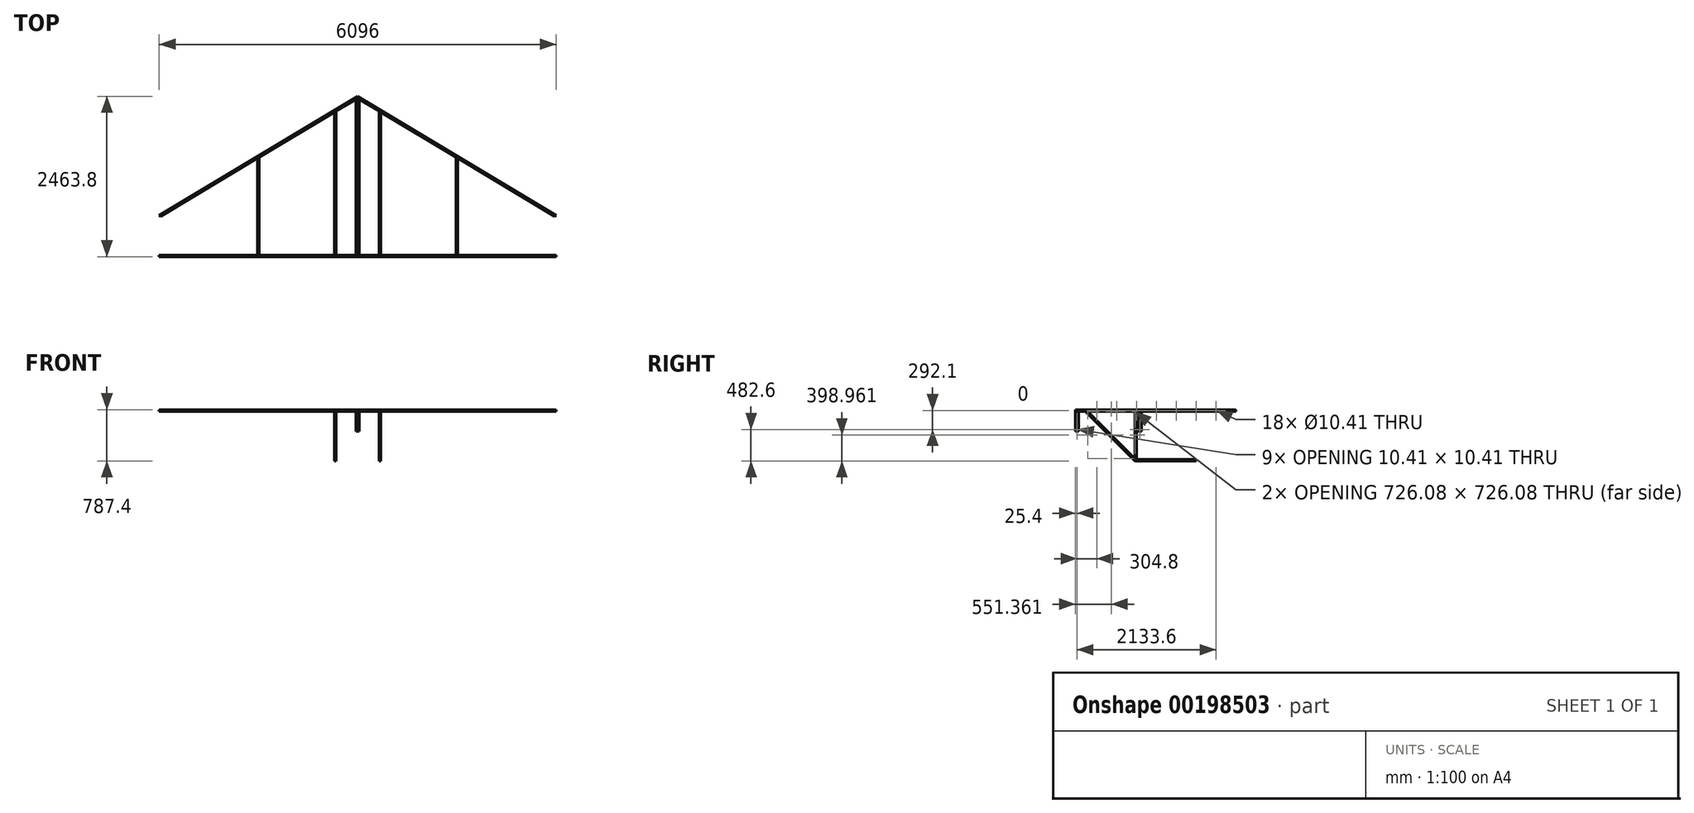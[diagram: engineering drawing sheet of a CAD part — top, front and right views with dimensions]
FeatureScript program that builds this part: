
annotation { "Feature Type Name" : "Feature", "Feature Type Description" : "" }
export const myFeature = defineFeature(function(context is Context, id is Id, definition is map)
    precondition{}
    {
        {
            var Q0;
            Q0=qCreatedBy(makeId("Top.planeOp"),FACE);
            var sketch = newSketch(context, id + "F0", { "sketchPlane" : qUnion([Q0])});
            skLineSegment(sketch, "E0.bottom", {"start": v(0, 0) * mm, "end": v(3048, 0) * mm});
            skLineSegment(sketch, "E0.top", {"start": v(0, 25.4) * mm, "end": v(3048, 25.4) * mm});
            skLineSegment(sketch, "E0.left", {"start": v(0, 0) * mm, "end": v(0, 25.4) * mm});
            skLineSegment(sketch, "E0.right", {"start": v(3048, 0) * mm, "end": v(3048, 25.4) * mm});
            skLineSegment(sketch, "E1.bottom", {"start": v(3048, 25.4) * mm, "end": v(3022.6, 25.4) * mm});
            skLineSegment(sketch, "E1.left", {"start": v(3048, 25.4) * mm, "end": v(3048, 635) * mm});
            skLineSegment(sketch, "E1.right", {"start": v(3022.6, 25.4) * mm, "end": v(3022.6, 620.62) * mm});
            skLineSegment(sketch, "E2", {"start": v(3048, 635) * mm, "end": v(3022.6, 620.62) * mm});
            skLineSegment(sketch, "E3", {"start": v(3048, 635) * mm, "end": v(0, 2463.8) * mm});
            skLineSegment(sketch, "E4", {"start": v(3022.6, 620.62) * mm, "end": v(25.4, 2418.94) * mm});
            skLineSegment(sketch, "E5", {"start": v(0, 25.4) * mm, "end": v(0, 2463.8) * mm});
            skLineSegment(sketch, "E6", {"start": v(0, 2463.8) * mm, "end": v(25.4, 2418.94) * mm});
            skLineSegment(sketch, "E7", {"start": v(25.4, 2418.94) * mm, "end": v(25.4, 25.4) * mm});
            skLineSegment(sketch, "E8", {"start": v(1511.3, 25.4) * mm, "end": v(1511.3, 1527.4) * mm});
            skLineSegment(sketch, "E9", {"start": v(1536.7, 1512.16) * mm, "end": v(1536.7, 25.4) * mm});
            skLineSegment(sketch, "E10", {"start": v(1511.3, 683.13) * mm, "end": v(1536.7, 683.13) * mm, "construction": true});
            skLineSegment(sketch, "E11", {"start": v(1524, 683.13) * mm, "end": v(1524, 25.4) * mm, "construction": true});
            skLineSegment(sketch, "E12", {"start": v(330.2, 25.4) * mm, "end": v(330.2, 2236.06) * mm});
            skLineSegment(sketch, "E13", {"start": v(355.6, 25.4) * mm, "end": v(355.6, 2220.82) * mm});
            skSolve(sketch);
        }
        {
            var Q0;
            {var subQ0=sQuery(id+"F0.wireOp",EDGE,"E5");Q0=makeQuery(id+"F0.imprint","IMPRINT",FACE,{"disambiguationData":[TD([[makeQuery(id+"F0.imprint","IMPRINT",EDGE,{"derivedFrom":subQ0}),-1.0]])]});}
            var Q1;
            {var subQ3=sQuery(id+"F0.wireOp",EDGE,"E2");Q1=makeQuery(id+"F0.imprint","IMPRINT",FACE,{"disambiguationData":[TD([[makeQuery(id+"F0.imprint","IMPRINT",EDGE,{"derivedFrom":subQ3}),-1.0]])]});}
            var Q2;
            {var subQ0=sQuery(id+"F0.wireOp",EDGE,"E8");Q2=makeQuery(id+"F0.imprint","IMPRINT",FACE,{"disambiguationData":[TD([[makeQuery(id+"F0.imprint","IMPRINT",EDGE,{"derivedFrom":subQ0}),-1.0]])]});}
            var Q3;
            Q3=makeQuery(id+"F0.imprint","IMPRINT",FACE,{"disambiguationData":[TD([[makeQuery(id+"F0.imprint","IMPRINT",EDGE,{"derivedFrom":sQuery(id+"F0.wireOp",EDGE,"E1.bottom")}),-1.0]])]});
            var Q4;
            Q4=makeQuery(id+"F0.imprint","IMPRINT",FACE,{"disambiguationData":[TD([[makeQuery(id+"F0.imprint","IMPRINT",EDGE,{"derivedFrom":sQuery(id+"F0.wireOp",EDGE,"E0.bottom")}),1.0]])]});
            var Q5;
            {var subQ0=sQuery(id+"F0.wireOp",EDGE,"E12");Q5=makeQuery(id+"F0.imprint","IMPRINT",FACE,{"disambiguationData":[TD([[makeQuery(id+"F0.imprint","IMPRINT",EDGE,{"derivedFrom":subQ0}),-1.0]])]});}
            extrude(context, id + "F1", {"entities" : qUnion([Q0, Q1, Q2, Q3, Q4, Q5]), "depth" : 25.4 * mm});
        }
        {
            var Q0;
            Q0=makeQuery(id+"F1.opExtrude","SWEPT_FACE",FACE,{"disambiguationData":[OSD([sQuery(id+"F0.wireOp",EDGE,"E0.bottom")])]});
            var sketch = newSketch(context, id + "F2", { "sketchPlane" : qUnion([Q0])});
            skLineSegment(sketch, "E14.0", {"start": v(0, 0) * mm, "end": v(3048, 0) * mm});
            skLineSegment(sketch, "E15", {"start": v(0, 0) * mm, "end": v(0, -304.8) * mm});
            skLineSegment(sketch, "E16", {"start": v(0, -304.8) * mm, "end": v(25.4, -304.8) * mm});
            skLineSegment(sketch, "E17", {"start": v(25.4, -304.8) * mm, "end": v(25.4, 0) * mm});
            skLineSegment(sketch, "E18", {"start": v(25.4, -279.4) * mm, "end": v(304.8, 0) * mm});
            skLineSegment(sketch, "E19", {"start": v(25.4, -243.48) * mm, "end": v(268.88, 0) * mm});
            skSolve(sketch);
        }
        {
            var Q0;
            {var subQ3=sQuery(id+"F2.wireOp",EDGE,"E15");Q0=makeQuery(id+"F2.imprint","IMPRINT",FACE,{"disambiguationData":[TD([[makeQuery(id+"F2.imprint","IMPRINT",EDGE,{"derivedFrom":subQ3}),1.0]])]});}
            extrude(context, id + "F3", {"entities" : qUnion([Q0]), "operationType" : NewBodyOperationType.ADD, "oppositeDirection" : true, "depth" : 50.8 * mm});
        }
        {
            var Q0;
            Q0=makeQuery(id+"F3.opExtrude","CAP_FACE",FACE,{"disambiguationData":[OSD([sQuery(id+"F2.wireOp",EDGE,"E14.0"),sQuery(id+"F2.wireOp",EDGE,"E15"),sQuery(id+"F2.wireOp",EDGE,"E16"),sQuery(id+"F2.wireOp",EDGE,"E17")])],"isStart":false});
            cPlane(context, id + "F4", {"entities" : qUnion([Q0]), "cplaneType" : CPlaneType.OFFSET, "offset" : 914.4 * mm, "width" : 152.4 * mm, "height" : 152.4 * mm});
        }
        {
            var Q0;
            Q0=qCreatedBy(id+"F4.planeOp",FACE);
            var sketch = newSketch(context, id + "F5", { "sketchPlane" : qUnion([Q0])});
            skLineSegment(sketch, "E20.0.0", {"start": v(0, 0) * mm, "end": v(-25.4, 0) * mm});
            skLineSegment(sketch, "E20.0.1", {"start": v(-25.4, 0) * mm, "end": v(-25.4, -304.8) * mm});
            skLineSegment(sketch, "E20.0.2", {"start": v(-25.4, -304.8) * mm, "end": v(0, -304.8) * mm});
            skLineSegment(sketch, "E20.0.3", {"start": v(0, -304.8) * mm, "end": v(0, 0) * mm});
            skSolve(sketch);
        }
        {
            var Q0;
            Q0 = qSketchRegion(id + "F5", true);
            extrude(context, id + "F6", {"entities" : qUnion([Q0]), "operationType" : NewBodyOperationType.ADD, "depth" : 50.8 * mm});
        }
        {
            var Q0;
            Q0=makeQuery(id+"F1.opExtrude","SWEPT_FACE",FACE,{"disambiguationData":[OSD([sQuery(id+"F0.wireOp",EDGE,"E12")])]});
            var sketch = newSketch(context, id + "F7", { "sketchPlane" : qUnion([Q0])});
            skLineSegment(sketch, "E21.0", {"start": v(-25.4, 0) * mm, "end": v(-2236.06, 0) * mm});
            skLineSegment(sketch, "E22", {"start": v(-939.8, 0) * mm, "end": v(-939.8, -762) * mm});
            skLineSegment(sketch, "E23", {"start": v(-939.8, -762) * mm, "end": v(-914.4, -762) * mm});
            skLineSegment(sketch, "E24", {"start": v(-914.4, -762) * mm, "end": v(-914.4, 0) * mm});
            skLineSegment(sketch, "E25", {"start": v(-914.4, -762) * mm, "end": v(-152.4, 0) * mm});
            skLineSegment(sketch, "E26", {"start": v(-152.4, 0) * mm, "end": v(-188.32, 0) * mm});
            skLineSegment(sketch, "E27", {"start": v(-188.32, 0) * mm, "end": v(-914.4, -726.08) * mm});
            skLineSegment(sketch, "E28", {"start": v(-939.8, -762) * mm, "end": v(-1854.2, -762) * mm});
            skLineSegment(sketch, "E29", {"start": v(-1854.2, -762) * mm, "end": v(-1854.2, -736.6) * mm});
            skLineSegment(sketch, "E30", {"start": v(-1854.2, -736.6) * mm, "end": v(-939.8, -736.6) * mm});
            skSolve(sketch);
        }
        {
            var Q0;
            {var subQ0=sQuery(id+"F7.wireOp",EDGE,"E25");Q0=makeQuery(id+"F7.imprint","IMPRINT",FACE,{"disambiguationData":[TD([[makeQuery(id+"F7.imprint","IMPRINT",EDGE,{"derivedFrom":subQ0}),1.0]])]});}
            var Q1;
            {var subQ0=sQuery(id+"F7.wireOp",EDGE,"E23");Q1=makeQuery(id+"F7.imprint","IMPRINT",FACE,{"disambiguationData":[TD([[makeQuery(id+"F7.imprint","IMPRINT",EDGE,{"derivedFrom":subQ0}),1.0]])]});}
            var Q2;
            {var subQ0=sQuery(id+"F7.wireOp",EDGE,"E28");Q2=makeQuery(id+"F7.imprint","IMPRINT",FACE,{"disambiguationData":[TD([[makeQuery(id+"F7.imprint","IMPRINT",EDGE,{"derivedFrom":subQ0}),-1.0]])]});}
            extrude(context, id + "F8", {"entities" : qUnion([Q0, Q1, Q2]), "operationType" : NewBodyOperationType.ADD, "oppositeDirection" : true, "depth" : 25.4 * mm});
        }
        {
            var Q0;
            Q0=makeQuery(id+"F6.boolean.opBoolean","MERGE",FACE,{"derivedFrom":[makeQuery(id+"F3.boolean.opBoolean","MERGE",FACE,{"derivedFrom":[makeQuery(id+"F1.opExtrude","SWEPT_FACE",FACE,{"disambiguationData":[OSD([sQuery(id+"F0.wireOp",EDGE,"E0.left"),sQuery(id+"F0.wireOp",EDGE,"E5")])]}),makeQuery(id+"F3.opExtrude","SWEPT_FACE",FACE,{"disambiguationData":[OSD([sQuery(id+"F2.wireOp",EDGE,"E15")])]})]}),makeQuery(id+"F6.opExtrude","SWEPT_FACE",FACE,{"disambiguationData":[OSD([sQuery(id+"F5.wireOp",EDGE,"E20.0.3")])]})]});
            var sketch = newSketch(context, id + "F9", { "sketchPlane" : qUnion([Q0])});
            skLineSegment(sketch, "E31", {"start": v(-2463.8, 12.7) * mm, "end": v(0, 12.7) * mm, "construction": true});
            skLineSegment(sketch, "E32", {"start": v(-25.4, -304.8) * mm, "end": v(-25.4, 25.4) * mm, "construction": true});
            skLineSegment(sketch, "E33", {"start": v(-990.6, -304.8) * mm, "end": v(-990.6, 25.4) * mm, "construction": true});
            skCircle(sketch, "E34", {"center": v(-2159, 12.7) * mm, "radius": 5.2 * mm});
            skCircle(sketch, "E35.1.0.0", {"center": v(-1854.2, 12.7) * mm, "radius": 5.2 * mm});
            skCircle(sketch, "E35.2.0.0", {"center": v(-1549.4, 12.7) * mm, "radius": 5.2 * mm});
            skLineSegment(sketch, "E35.direction1", {"start": v(-2159, 12.7) * mm, "end": v(-1854.2, 12.7) * mm, "construction": true});
            skCircle(sketch, "E36.0.3.0", {"center": v(-1244.6, 12.7) * mm, "radius": 5.2 * mm});
            skCircle(sketch, "E36.0.4.0", {"center": v(-939.8, 12.7) * mm, "radius": 5.2 * mm});
            skCircle(sketch, "E36.0.5.0", {"center": v(-635, 12.7) * mm, "radius": 5.2 * mm});
            skCircle(sketch, "E36.0.6.0", {"center": v(-330.2, 12.7) * mm, "radius": 5.2 * mm});
            skCircle(sketch, "E37", {"center": v(-990.6, -279.4) * mm, "radius": 5.2 * mm});
            skCircle(sketch, "E38", {"center": v(-25.4, -279.4) * mm, "radius": 5.2 * mm});
            skSolve(sketch);
        }
        {
            var Q0;
            Q0=makeQuery(id+"F9.imprint","IMPRINT",FACE,{"disambiguationData":[TD([[makeQuery(id+"F9.imprint","IMPRINT",EDGE,{"derivedFrom":sQuery(id+"F9.wireOp",EDGE,"E34")}),1.0]])]});
            var Q1;
            Q1=makeQuery(id+"F9.imprint","IMPRINT",FACE,{"disambiguationData":[TD([[makeQuery(id+"F9.imprint","IMPRINT",EDGE,{"derivedFrom":sQuery(id+"F9.wireOp",EDGE,"E35.1.0.0")}),1.0]])]});
            var Q2;
            Q2=makeQuery(id+"F9.imprint","IMPRINT",FACE,{"disambiguationData":[TD([[makeQuery(id+"F9.imprint","IMPRINT",EDGE,{"derivedFrom":sQuery(id+"F9.wireOp",EDGE,"E35.2.0.0")}),1.0]])]});
            var Q3;
            Q3=makeQuery(id+"F9.imprint","IMPRINT",FACE,{"disambiguationData":[TD([[makeQuery(id+"F9.imprint","IMPRINT",EDGE,{"derivedFrom":sQuery(id+"F9.wireOp",EDGE,"E36.0.3.0")}),1.0]])]});
            var Q4;
            Q4=makeQuery(id+"F9.imprint","IMPRINT",FACE,{"disambiguationData":[TD([[makeQuery(id+"F9.imprint","IMPRINT",EDGE,{"derivedFrom":sQuery(id+"F9.wireOp",EDGE,"E36.0.4.0")}),1.0]])]});
            var Q5;
            Q5=makeQuery(id+"F9.imprint","IMPRINT",FACE,{"disambiguationData":[TD([[makeQuery(id+"F9.imprint","IMPRINT",EDGE,{"derivedFrom":sQuery(id+"F9.wireOp",EDGE,"E37")}),1.0]])]});
            var Q6;
            Q6=makeQuery(id+"F9.imprint","IMPRINT",FACE,{"disambiguationData":[TD([[makeQuery(id+"F9.imprint","IMPRINT",EDGE,{"derivedFrom":sQuery(id+"F9.wireOp",EDGE,"E36.0.5.0")}),1.0]])]});
            var Q7;
            Q7=makeQuery(id+"F9.imprint","IMPRINT",FACE,{"disambiguationData":[TD([[makeQuery(id+"F9.imprint","IMPRINT",EDGE,{"derivedFrom":sQuery(id+"F9.wireOp",EDGE,"E36.0.6.0")}),1.0]])]});
            var Q8;
            Q8=makeQuery(id+"F9.imprint","IMPRINT",FACE,{"disambiguationData":[TD([[makeQuery(id+"F9.imprint","IMPRINT",EDGE,{"derivedFrom":sQuery(id+"F9.wireOp",EDGE,"E38")}),1.0]])]});
            extrude(context, id + "F10", {"entities" : qUnion([Q0, Q1, Q2, Q3, Q4, Q5, Q6, Q7, Q8]), "operationType" : NewBodyOperationType.REMOVE, "endBound" : BoundingType.UP_TO_NEXT, "oppositeDirection" : true, "depth" : 25.4 * mm});
        }
        {
            var Q0;
            Q0=makeQuery(id+"F1.opExtrude","SWEPT_BODY",BODY,{"disambiguationData":[OSD([sQuery(id+"F0.wireOp",EDGE,"E0.bottom"),sQuery(id+"F0.wireOp",EDGE,"E0.top"),sQuery(id+"F0.wireOp",EDGE,"E0.left"),sQuery(id+"F0.wireOp",EDGE,"E0.right"),sQuery(id+"F0.wireOp",EDGE,"E1.left"),sQuery(id+"F0.wireOp",EDGE,"E1.right"),sQuery(id+"F0.wireOp",EDGE,"E3"),sQuery(id+"F0.wireOp",EDGE,"E4"),sQuery(id+"F0.wireOp",EDGE,"E5"),sQuery(id+"F0.wireOp",EDGE,"E7"),sQuery(id+"F0.wireOp",EDGE,"E8"),sQuery(id+"F0.wireOp",EDGE,"E9"),sQuery(id+"F0.wireOp",EDGE,"E12"),sQuery(id+"F0.wireOp",EDGE,"E13")])]});
            var Q1;
            Q1=makeQuery(id+"F6.boolean.opBoolean","MERGE",FACE,{"derivedFrom":[makeQuery(id+"F3.boolean.opBoolean","MERGE",FACE,{"derivedFrom":[makeQuery(id+"F1.opExtrude","SWEPT_FACE",FACE,{"disambiguationData":[OSD([sQuery(id+"F0.wireOp",EDGE,"E0.left"),sQuery(id+"F0.wireOp",EDGE,"E5")])]}),makeQuery(id+"F3.opExtrude","SWEPT_FACE",FACE,{"disambiguationData":[OSD([sQuery(id+"F2.wireOp",EDGE,"E15")])]})]}),makeQuery(id+"F6.opExtrude","SWEPT_FACE",FACE,{"disambiguationData":[OSD([sQuery(id+"F5.wireOp",EDGE,"E20.0.3")])]})]});
            mirror(context, id + "F11", {"entities" : qUnion([Q0]), "mirrorPlane" : qUnion([Q1])});
        }
    });
